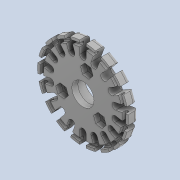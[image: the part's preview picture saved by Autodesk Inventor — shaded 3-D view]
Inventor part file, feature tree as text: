
AUTODESK INVENTOR PART (.ipt)
format: ipt  version: 2020.4 (Build 244396000, 396)  size: 682,496 bytes
history: native  units: mm
features: sketch x8, extrude x7, hole x1, fillet x1
ambient origin geometry x8: Origin, YZ Plane, XZ Plane, XY Plane, X Axis, Y Axis, Z Axis, Center Point
bodies: Solid1 (feature_tree)
feature tree (17):
  extrude  "PartA Base"  Depth=7.0mm TaperAngle=0.0deg
  extrude  "Shaft Entrance"  Depth=2.0mm TaperAngle=0.0deg
  extrude  "Roller Entrance"  TaperAngle=90.0deg  [1 undecoded]
  extrude  "Wire Entrance"  TaperAngle=0.0deg  [1 undecoded]
  hole  "Bearing Fit"  [1 undecoded]
  extrude  "Threads and Gear Fit"  Depth=40.8mm
  extrude  "M3 Nut"  Depth=42.52mm
  fillet  "Wire and Ground Rounding"  Radius=2.1mm
  extrude  "Extrusion7"  Depth=10.0mm
  sketch  "Sketch1"  dims[d0=45.0mm d1=7.0mm d2=0.0mm]
  sketch  "Sketch2"  dims[d3=27.0mm d4=2.0mm d5=0.0mm]
  sketch  "Sketch3"  dims[d6=6.7mm d7=90.0deg]
  sketch  "Sketch4"  dims[d8=3.2mm d9=0.0mm]
  sketch  "Sketch5"  dims[d10=19.6mm d11=10.0mm d12=0.0mm]
  sketch  "Sketch6"  dims[d13=180.0mm d15=360.0deg d17=40.8mm]
  sketch  "Sketch7"  dims[d18=39.08mm d19=42.52mm d20=2.1mm d21=0.0mm]
  sketch  "Sketch8"  dims[d22=11.0mm d23=6.0mm d24=4.0mm d25=2.0mm d26=90.0deg d27=3.0mm d28=0.0mm d29=3.0mm d30=1.91013mm d31=10.833mm d32=30.0mm d34=360.0deg d36=12.0mm d37=10.0mm d38=0.0mm d39=2.76mm d40=2.76mm d41=2.76mm d42=2.55mm d43=0.0mm d44=2.0mm d45=0.625mm d46=12.0mm d47=10.0mm d48=0.0mm]
note: 3 required parameter values undecoded (feature->parameter linkage not recoverable at this tier; creation-order binding heuristic only, values carry confidence <= 0.55)
